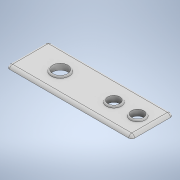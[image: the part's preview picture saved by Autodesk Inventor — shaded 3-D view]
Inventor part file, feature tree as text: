
AUTODESK INVENTOR PART (.ipt)
format: ipt  version: 2021 (Build 250183000, 183)  size: 179,200 bytes
history: native  units: mm
features: extrude x5, sketch x5, fillet x3
ambient origin geometry x8: Origin, YZ Plane, XZ Plane, XY Plane, X Axis, Y Axis, Z Axis, Center Point
bodies: Solid1 (feature_tree)
feature tree (13):
  extrude  "Extrusion1"  Depth=60.0mm
  sketch  "Sketch2"  dims[d2=2.5mm d3=0.0mm d4=20.0mm]
  extrude  "Extrusion2"  Depth=2.5mm
  extrude  "Extrusion3"  Depth=200.0mm
  fillet  "Fillet1"  Radius=40.0mm
  fillet  "Fillet2"  Radius=200.0mm
  extrude  "Extrusion4"  Depth=5.0mm
  extrude  "Extrusion5"  Depth=5.0mm
  fillet  "Fillet3"  Radius=5.0mm
  sketch  "Sketch1"  dims[d0=200.0mm d1=60.0mm]
  sketch  "Sketch4"  dims[d5=30.0mm d6=20.0mm d7=40.0mm d8=200.0mm]
  sketch  "Sketch5"  dims[d9=5.0mm d10=5.0mm]
  sketch  "Sketch6"  dims[d11=70.0mm d12=5.0mm d13=5.0mm d14=0.0mm d15=7.5mm d16=0.0mm d17=5.0mm d18=5.0mm d19=50.0mm d20=25.0mm d21=7.5mm d22=0.0mm d23=30.0mm d24=25.0mm d25=2.5mm d26=0.0mm d27=2.5mm]
